# Revit family: FP_Revit_18_HBD1200e_External_Blower_90001866A
name_source: partatom
category: Specialty Equipment
revit_build: Autodesk Revit 2018 (Build: 20170223_1515(x64)
units: mm (PartAtom-declared; Revit-internal decimal feet)

## family parameters
Always vertical = Yes
Cut with Voids When Loaded = Yes
OmniClass Number = 23.40.40.00
OmniClass Title = Food Service Equipment and Furnishings
Part Type = Normal
Room Calculation Point = No
Round Connector Dimension = Use Diameter
Shared = No
Work Plane-Based = No

## types (1)
- FP_Revit_18_HBD1200e_External_Blower_90001866A
    Cavity - Height = 864 mm  [stored 2.83465 ft]
    Cavity - Width = 600 mm
    Chassis - Depth = 195 mm  [stored 0.639764 ft]
    Chassis - Height = 803 mm  [stored 2.63451 ft]
    Chassis - Width = 635 mm
    Connector Description - Electrical = 120 V, 60 Hz, 2.8 A
    Connector Description - Extraction = 10” (254 mm) ducting, 1200 CFM
    Description = External Blower
    Manufacturer = Fisher & Paykel Appliances
    Material - Body = Fisher & Paykel - Grey
    Model = HPD1200E
    Product - Depth = 227 mm  [stored 0.744751 ft]
    Product - Height = 845 mm  [stored 2.77231 ft]
    Product - Width = 680 mm  [stored 2.23097 ft]
    URL = www.fisherpaykel.com
    Visibility - Clearance Required = Yes

note: [stored X ft] marks values corroborated as IEEE doubles in the binary element streams (Revit-internal decimal feet)

## geometry (parser evidence)
native form markers: Sweep x2
no freeform markers — native parametric forms only
